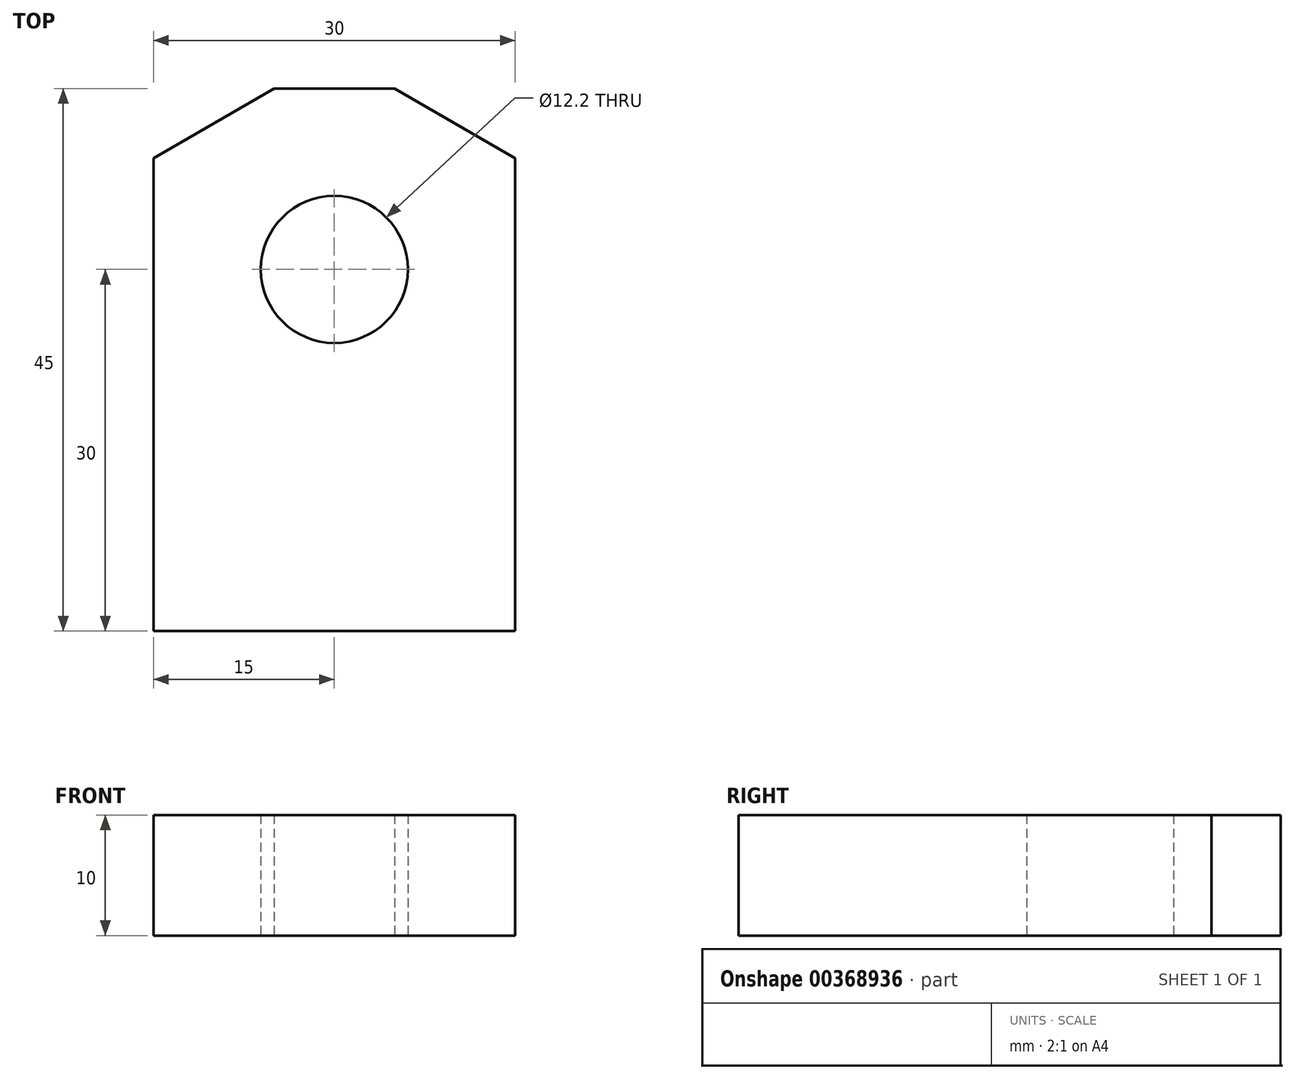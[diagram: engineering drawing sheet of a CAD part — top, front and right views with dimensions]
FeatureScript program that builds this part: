
annotation { "Feature Type Name" : "Feature", "Feature Type Description" : "" }
export const myFeature = defineFeature(function(context is Context, id is Id, definition is map)
    precondition{}
    {
        {
            var Q0;
            Q0=qCreatedBy(makeId("Top.planeOp"),FACE);
            var sketch = newSketch(context, id + "F0", { "sketchPlane" : qUnion([Q0])});
            skLineSegment(sketch, "E0.bottom", {"start": v(0, 0) * mm, "end": v(30, 0) * mm});
            skLineSegment(sketch, "E0.top", {"start": v(10, 45) * mm, "end": v(20, 45) * mm});
            skLineSegment(sketch, "E0.left", {"start": v(0, 0) * mm, "end": v(0, 39.23) * mm});
            skLineSegment(sketch, "E0.right", {"start": v(30, 0) * mm, "end": v(30, 39.23) * mm});
            skLineSegment(sketch, "E1", {"start": v(10, 45) * mm, "end": v(0, 39.23) * mm});
            skLineSegment(sketch, "E2", {"start": v(30, 39.23) * mm, "end": v(20, 45) * mm});
            skCircle(sketch, "E3", {"center": v(15, 30) * mm, "radius": 6.1 * mm});
            skPoint(sketch, "E3.centerSnap0", {"position": v(15, 45) * mm});
            skPoint(sketch, "E4.orphan", {"position": v(0, 45) * mm});
            skPoint(sketch, "E5.orphan", {"position": v(30, 45) * mm});
            skSolve(sketch);
        }
        {
            var Q0;
            Q0=qSketchRegion(id+"F0",true);
            extrude(context, id + "F1", {"entities" : qUnion([Q0]), "depth" : 10 * mm});
        }
    });
